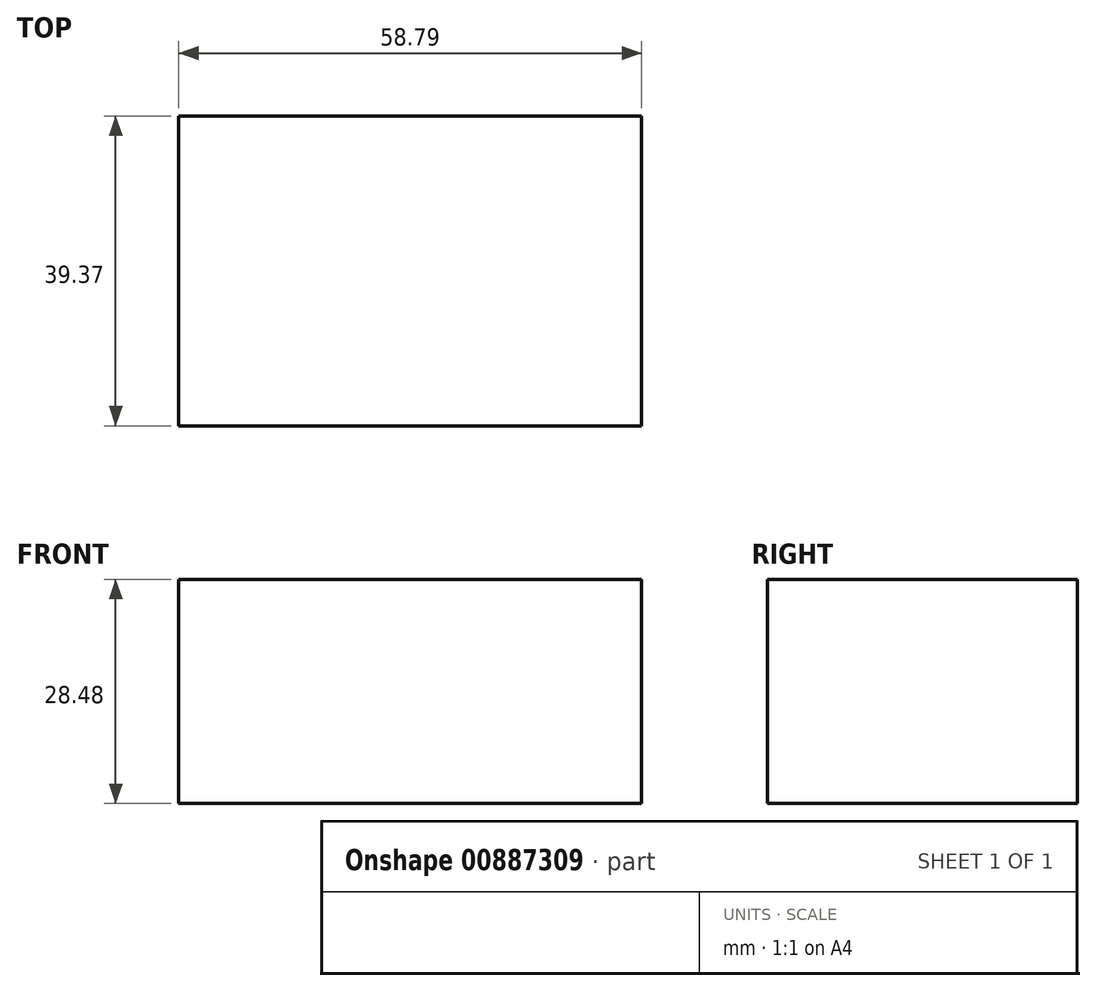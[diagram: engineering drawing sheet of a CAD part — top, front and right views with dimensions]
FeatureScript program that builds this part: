
annotation { "Feature Type Name" : "Feature", "Feature Type Description" : "" }
export const myFeature = defineFeature(function(context is Context, id is Id, definition is map)
    precondition{}
    {
        {
            var Q0;
            Q0=qCreatedBy(makeId("Front.planeOp"),FACE);
            var sketch = newSketch(context, id + "F0", { "sketchPlane" : qUnion([Q0])});
            skLineSegment(sketch, "E0.bottom", {"start": v(-25.35, 14.15) * mm, "end": v(33.44, 14.15) * mm});
            skLineSegment(sketch, "E0.top", {"start": v(-25.35, -14.33) * mm, "end": v(33.44, -14.33) * mm});
            skLineSegment(sketch, "E0.left", {"start": v(-25.35, 14.15) * mm, "end": v(-25.35, -14.33) * mm});
            skLineSegment(sketch, "E0.right", {"start": v(33.44, 14.15) * mm, "end": v(33.44, -14.33) * mm});
            skSolve(sketch);
        }
        {
            var Q0;
            Q0 = qSketchRegion(id + "F0", true);
            extrude(context, id + "F1", {"entities" : qUnion([Q0]), "depth" : 39.37 * mm, "offsetDistance" : 25.4 * mm});
        }
    });
